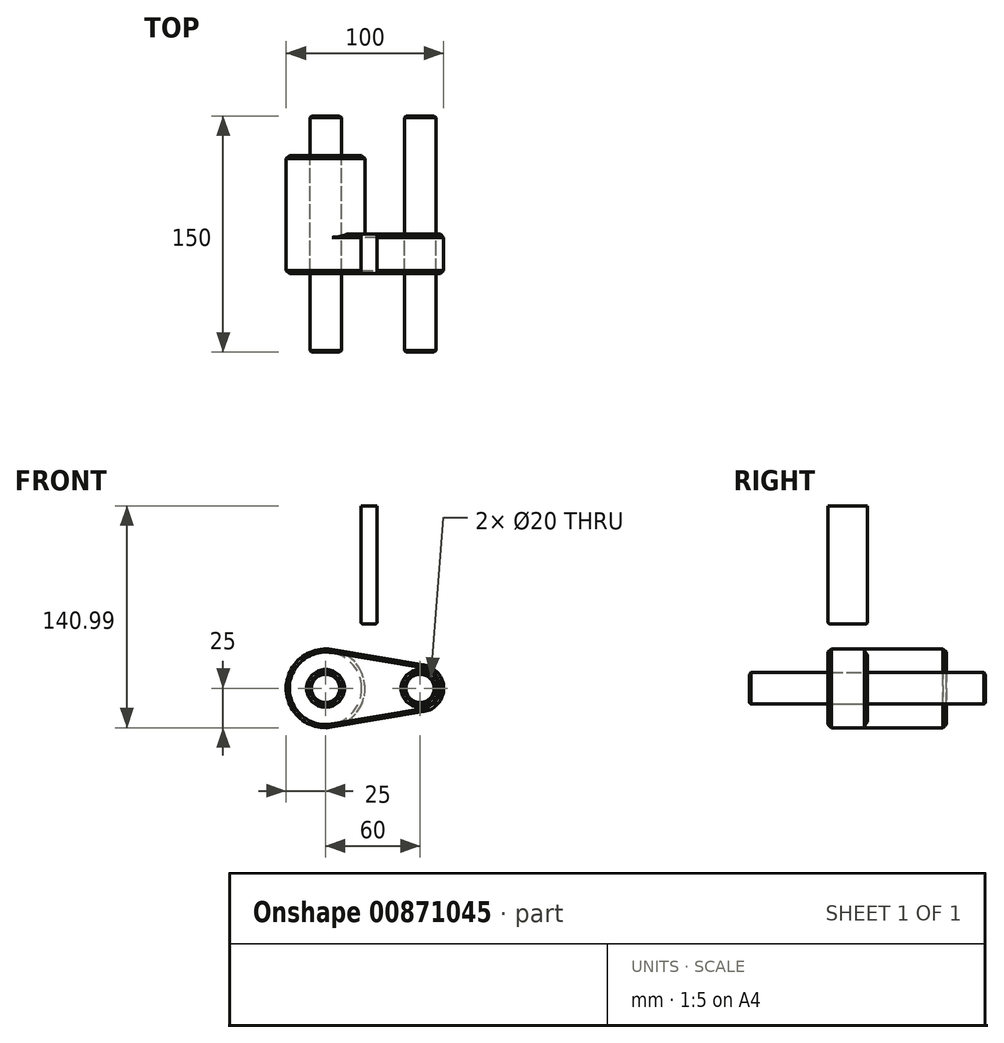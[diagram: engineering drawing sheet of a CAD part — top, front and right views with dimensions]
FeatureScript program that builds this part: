
annotation { "Feature Type Name" : "Feature", "Feature Type Description" : "" }
export const myFeature = defineFeature(function(context is Context, id is Id, definition is map)
    precondition{}
    {
        {
            var Q0;
            Q0=qCreatedBy(makeId("Front.planeOp"),FACE);
            var sketch = newSketch(context, id + "F0", { "sketchPlane" : qUnion([Q0])});
            skCircle(sketch, "E0", {"center": v(0, 0) * mm, "radius": 25 * mm});
            skCircle(sketch, "E1", {"center": v(60, 0) * mm, "radius": 15 * mm});
            skCircle(sketch, "E2", {"center": v(0, 0) * mm, "radius": 10 * mm});
            skCircle(sketch, "E3", {"center": v(60, 0) * mm, "radius": 10 * mm});
            skLineSegment(sketch, "E4", {"start": v(4.17, -24.65) * mm, "end": v(62.5, -14.8) * mm});
            skLineSegment(sketch, "E5", {"start": v(4.17, 24.65) * mm, "end": v(62.5, 14.8) * mm});
            skSolve(sketch);
        }
        {
            var Q0;
            Q0 = qSketchRegion(id + "F0", true);
            extrude(context, id + "F1", {"entities" : qUnion([Q0]), "depth" : 25 * mm, "offsetDistance" : 25 * mm});
        }
        {
            var Q0;
            Q0=makeQuery(id+"F0.imprint","IMPRINT",FACE,{"disambiguationData":[TD([[makeQuery(id+"F0.imprint","IMPRINT",EDGE,{"derivedFrom":sQuery(id+"F0.wireOp",EDGE,"E2")}),-1.0]])]});
            extrude(context, id + "F2", {"entities" : qUnion([Q0]), "operationType" : NewBodyOperationType.ADD, "oppositeDirection" : true, "depth" : 50 * mm, "offsetDistance" : 25 * mm});
        }
        {
            var Q0;
            Q0=makeQuery(id+"F1.opExtrude","CAP_FACE",FACE,{"disambiguationData":[OSD([sQuery(id+"F0.wireOp",EDGE,"E0"),sQuery(id+"F0.wireOp",EDGE,"E1"),sQuery(id+"F0.wireOp",EDGE,"E2"),sQuery(id+"F0.wireOp",EDGE,"E3"),sQuery(id+"F0.wireOp",EDGE,"37d62399-3308-4b92-bfca-0fc7045b6e15"),sQuery(id+"F0.wireOp",EDGE,"f4f203ae-778c-4323-8132-5ffa81ed7b3d")])],"isStart":false});
            chamfer(context, id + "F3", {"entities" : qUnion([Q0]), "width" : 2 * mm, "tangentPropagation" : true});
        }
        {
            var Q0;
            Q0=makeQuery(id+"F2.opExtrude","CAP_EDGE",EDGE,{"disambiguationData":[OSD([sQuery(id+"F0.wireOp",EDGE,"E2")])],"isStart":false});
            var Q1;
            Q1=makeQuery(id+"F2.opExtrude","CAP_FACE",FACE,{"disambiguationData":[OSD([sQuery(id+"F0.wireOp",EDGE,"E0"),sQuery(id+"F0.wireOp",EDGE,"E2")])],"isStart":false});
            chamfer(context, id + "F4", {"entities" : qUnion([Q0, Q1]), "width" : 2 * mm, "tangentPropagation" : true});
        }
        {
            var Q0;
            Q0=makeQuery(id+"F1.opExtrude","CAP_EDGE",EDGE,{"disambiguationData":[OSD([sQuery(id+"F0.wireOp",EDGE,"E5")])],"isStart":true});
            var Q1;
            Q1=makeQuery(id+"F1.opExtrude","CAP_EDGE",EDGE,{"disambiguationData":[OSD([sQuery(id+"F0.wireOp",EDGE,"E3")])],"isStart":true});
            chamfer(context, id + "F5", {"entities" : qUnion([Q0, Q1]), "width" : 2 * mm, "tangentPropagation" : true});
        }
        {
            var Q0;
            Q0=qCreatedBy(makeId("Front.planeOp"),FACE);
            var sketch = newSketch(context, id + "F6", { "sketchPlane" : qUnion([Q0])});
            skCircle(sketch, "E6", {"center": v(60, 0) * mm, "radius": 10 * mm});
            skSolve(sketch);
        }
        {
            var Q0;
            Q0 = qSketchRegion(id + "F6", true);
            extrude(context, id + "F7", {"entities" : qUnion([Q0]), "endBound" : BoundingType.SYMMETRIC, "depth" : 150 * mm, "offsetDistance" : 25 * mm});
        }
        {
            var Q0;
            Q0=makeQuery(id+"F7.opExtrude","CAP_FACE",FACE,{"disambiguationData":[OSD([sQuery(id+"F6.wireOp",EDGE,"E6")])],"isStart":false});
            chamfer(context, id + "F8", {"entities" : qUnion([Q0]), "width" : 1 * mm, "tangentPropagation" : true});
        }
        {
            var Q0;
            Q0=makeQuery(id+"F7.opExtrude","CAP_EDGE",EDGE,{"disambiguationData":[OSD([sQuery(id+"F6.wireOp",EDGE,"E6")])],"isStart":true});
            chamfer(context, id + "F9", {"entities" : qUnion([Q0]), "width" : 1 * mm, "tangentPropagation" : true});
        }
        {
            var Q0;
            Q0 = qSketchRegion(id + "F6", true);
            var sketch = newSketch(context, id + "F10", { "sketchPlane" : qUnion([Q0])});
            skCircle(sketch, "E7", {"center": v(0, 0) * mm, "radius": 10 * mm});
            skSolve(sketch);
        }
        {
            var Q0;
            Q0 = qSketchRegion(id + "F10", true);
            extrude(context, id + "F11", {"entities" : qUnion([Q0]), "endBound" : BoundingType.SYMMETRIC, "depth" : 150 * mm, "offsetDistance" : 25 * mm});
        }
        {
            var Q0;
            Q0=makeQuery(id+"F11.opExtrude","CAP_EDGE",EDGE,{"disambiguationData":[OSD([sQuery(id+"F10.wireOp",EDGE,"E7")])],"isStart":false});
            chamfer(context, id + "F12", {"entities" : qUnion([Q0]), "width" : 1 * mm, "tangentPropagation" : true});
        }
        {
            var Q0;
            Q0=makeQuery(id+"F11.opExtrude","CAP_EDGE",EDGE,{"disambiguationData":[OSD([sQuery(id+"F10.wireOp",EDGE,"E7")])],"isStart":true});
            chamfer(context, id + "F13", {"entities" : qUnion([Q0]), "width" : 1 * mm, "tangentPropagation" : true});
        }
        {
            var Q0;
            Q0=qCreatedBy(makeId("Front.planeOp"),FACE);
            var sketch = newSketch(context, id + "F14", { "sketchPlane" : qUnion([Q0])});
            skLineSegment(sketch, "E8.bottom", {"start": v(22.6, 115.99) * mm, "end": v(32.6, 115.99) * mm});
            skLineSegment(sketch, "E8.top", {"start": v(22.6, 40.99) * mm, "end": v(32.6, 40.99) * mm});
            skLineSegment(sketch, "E8.left", {"start": v(22.6, 115.99) * mm, "end": v(22.6, 40.99) * mm});
            skLineSegment(sketch, "E8.right", {"start": v(32.6, 115.99) * mm, "end": v(32.6, 40.99) * mm});
            skSolve(sketch);
        }
        {
            var Q0;
            Q0=makeQuery(id+"F14.imprint","IMPRINT",FACE,{"disambiguationData":[TD([[makeQuery(id+"F14.imprint","IMPRINT",EDGE,{"derivedFrom":sQuery(id+"F14.wireOp",EDGE,"E8.bottom")}),-1.0]])]});
            extrude(context, id + "F15", {"entities" : qUnion([Q0]), "depth" : 25 * mm, "offsetDistance" : 25 * mm});
        }
        {
            var Q0;
            Q0=makeQuery(id+"F15.opExtrude","SWEPT_FACE",FACE,{"disambiguationData":[OSD([sQuery(id+"F14.wireOp",EDGE,"E8.top")])]});
            fillet(context, id + "F16", {"entities" : qUnion([Q0]), "radius" : 1 * mm, "allowEdgeOverflow" : false});
        }
    });
